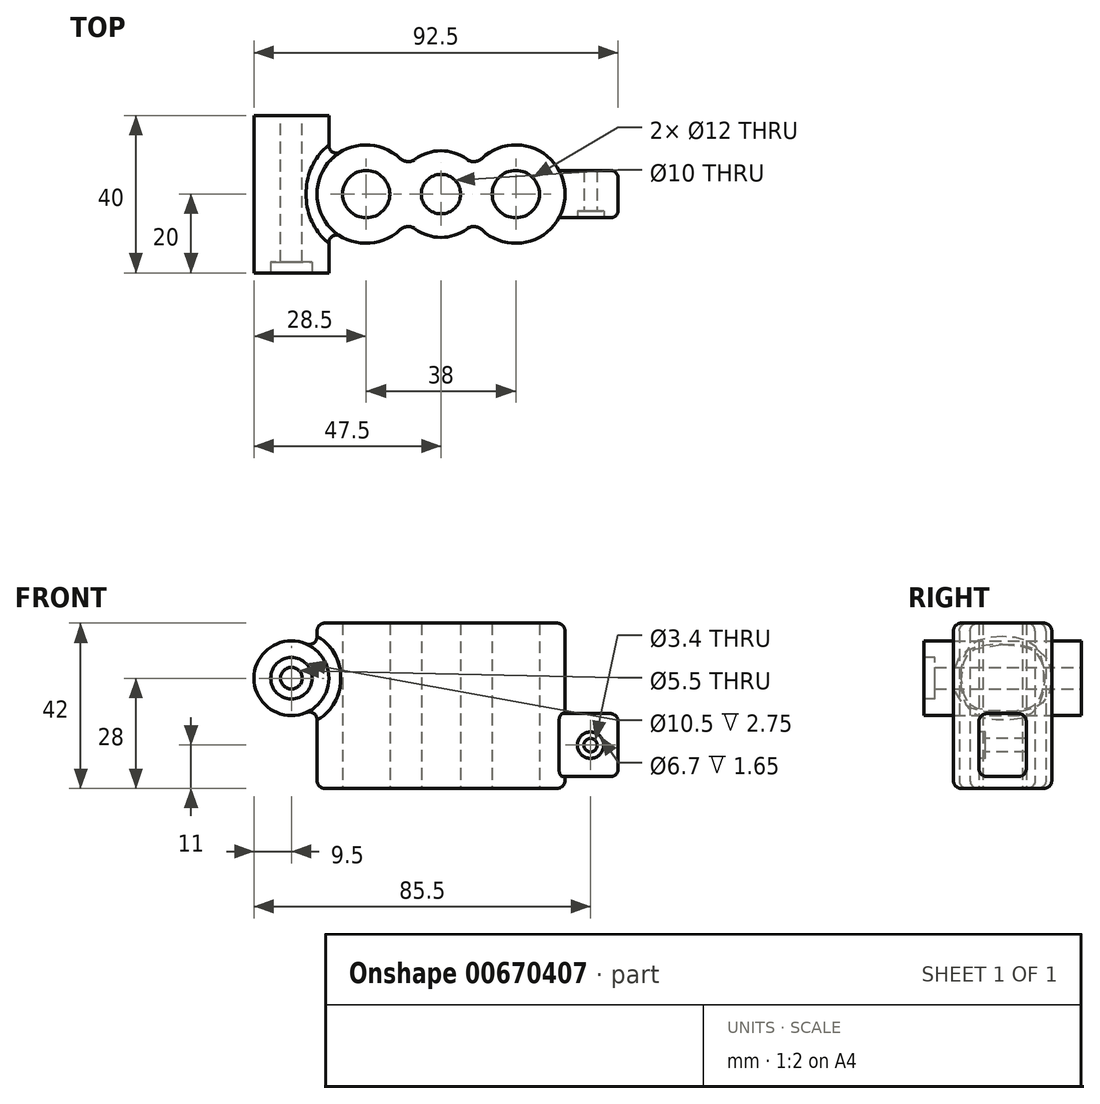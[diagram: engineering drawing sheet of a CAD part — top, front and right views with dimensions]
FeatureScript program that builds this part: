
annotation { "Feature Type Name" : "Feature", "Feature Type Description" : "" }
export const myFeature = defineFeature(function(context is Context, id is Id, definition is map)
    precondition{}
    {
        {
            var Q0;
            Q0=qCreatedBy(makeId("Top.planeOp"),FACE);
            var sketch = newSketch(context, id + "F0", { "sketchPlane" : qUnion([Q0])});
            skLineSegment(sketch, "E0", {"start": v(-22.84, 0) * mm, "end": v(30.08, 0) * mm, "construction": true});
            skLineSegment(sketch, "E1", {"start": v(0, 24.49) * mm, "end": v(0, -24.27) * mm, "construction": true});
            skCircle(sketch, "E2", {"center": v(0, 0) * mm, "radius": 5 * mm});
            skCircle(sketch, "E3", {"center": v(19, 0) * mm, "radius": 6 * mm});
            skCircle(sketch, "E4", {"center": v(-19, 0) * mm, "radius": 6 * mm});
            skArc(sketch, "E5", {"start": v(-10.4, 9.07) * mm, "mid": v(-31.5, 0) * mm, "end": v(-10.4, -9.07) * mm});
            skArc(sketch, "E6", {"start": v(-6.55, -8.84) * mm, "mid": v(0, -11) * mm, "end": v(6.55, -8.84) * mm});
            skArc(sketch, "E7", {"start": v(10.4, -9.07) * mm, "mid": v(31.5, 0) * mm, "end": v(10.4, 9.07) * mm});
            skArc(sketch, "E8.trimOffspring", {"start": v(6.55, 8.84) * mm, "mid": v(0, 11) * mm, "end": v(-6.55, 8.84) * mm});
            skPoint(sketch, "E9.visualSharp", {"position": v(-8.57, 6.9) * mm});
            skArc(sketch, "E9.filletArc", {"start": v(-10.4, 9.07) * mm, "mid": v(-8.52, 8.25) * mm, "end": v(-6.55, 8.84) * mm});
            skPoint(sketch, "E10.visualSharp", {"position": v(8.57, 6.9) * mm});
            skArc(sketch, "E10.filletArc", {"start": v(6.55, 8.84) * mm, "mid": v(8.52, 8.25) * mm, "end": v(10.4, 9.07) * mm});
            skPoint(sketch, "E11.visualSharp", {"position": v(8.57, -6.9) * mm});
            skArc(sketch, "E11.filletArc", {"start": v(10.4, -9.07) * mm, "mid": v(8.52, -8.25) * mm, "end": v(6.55, -8.84) * mm});
            skPoint(sketch, "E12.visualSharp", {"position": v(-8.57, -6.9) * mm});
            skArc(sketch, "E12.filletArc", {"start": v(-6.55, -8.84) * mm, "mid": v(-8.52, -8.25) * mm, "end": v(-10.4, -9.07) * mm});
            skSolve(sketch);
        }
        {
            var Q0;
            Q0=makeQuery(id+"F0.imprint","IMPRINT",FACE,{"disambiguationData":[TD([[makeQuery(id+"F0.imprint","IMPRINT",EDGE,{"derivedFrom":sQuery(id+"F0.wireOp",EDGE,"E2")}),-1.0]])]});
            extrude(context, id + "F1", {"entities" : qUnion([Q0]), "depth" : 42 * mm, "offsetDistance" : 25 * mm});
        }
        {
            var Q0;
            Q0=qCreatedBy(makeId("Front.planeOp"),FACE);
            var sketch = newSketch(context, id + "F2", { "sketchPlane" : qUnion([Q0])});
            skLineSegment(sketch, "E13", {"start": v(-30.33, 0) * mm, "end": v(35.68, 0) * mm, "construction": true});
            skLineSegment(sketch, "E14", {"start": v(0, -22.77) * mm, "end": v(0, 37.59) * mm, "construction": true});
            skCircle(sketch, "E15", {"center": v(-38, 28) * mm, "radius": 2.75 * mm});
            skCircle(sketch, "E16", {"center": v(-38, 28) * mm, "radius": 9.5 * mm});
            skLineSegment(sketch, "E17", {"start": v(-85.83, 21) * mm, "end": v(126.07, 21) * mm, "construction": true});
            skSolve(sketch);
        }
        {
            var Q0;
            Q0=makeQuery(id+"F2.imprint","IMPRINT",FACE,{"disambiguationData":[TD([[makeQuery(id+"F2.imprint","IMPRINT",EDGE,{"derivedFrom":sQuery(id+"F2.wireOp",EDGE,"E15")}),-1.0]])]});
            extrude(context, id + "F3", {"entities" : qUnion([Q0]), "operationType" : NewBodyOperationType.ADD, "endBound" : BoundingType.SYMMETRIC, "depth" : 40 * mm, "offsetDistance" : 25 * mm});
        }
        {
            var Q0;
            Q0=makeQuery(id+"F3.opExtrude","CAP_FACE",FACE,{"disambiguationData":[OSD([sQuery(id+"F2.wireOp",EDGE,"E15"),sQuery(id+"F2.wireOp",EDGE,"E16")])],"isStart":false});
            var sketch = newSketch(context, id + "F4", { "sketchPlane" : qUnion([Q0])});
            skCircle(sketch, "E18", {"center": v(-38, 28) * mm, "radius": 5.25 * mm});
            skSolve(sketch);
        }
        {
            var Q0;
            Q0=makeQuery(id+"F4.imprint","IMPRINT",FACE,{"disambiguationData":[TD([[makeQuery(id+"F4.imprint","IMPRINT",EDGE,{"derivedFrom":sQuery(id+"F4.wireOp",EDGE,"E18")}),1.0]])]});
            var Q1;
            Q1=sQuery(id+"F4.wireOp",EDGE,"E18");
            extrude(context, id + "F5", {"entities" : qUnion([Q0]), "operationType" : NewBodyOperationType.REMOVE, "surfaceEntities" : qUnion([Q1]), "oppositeDirection" : true, "depth" : 2.75 * mm, "offsetDistance" : 25 * mm});
        }
        {
            var Q0;
            Q0=qCreatedBy(makeId("Right.planeOp"),FACE);
            var Q1;
            Q1=sQuery(id+"F4.wireOp",VERTEX,"E18.center");
            cPlane(context, id + "F6", {"entities" : qUnion([Q0, Q1]), "cplaneType" : CPlaneType.PLANE_POINT, "offset" : 25 * mm, "width" : 150 * mm, "height" : 150 * mm});
        }
        {
            var Q0;
            Q0=qCreatedBy(id+"F6.planeOp",FACE);
            cPlane(context, id + "F7", {"entities" : qUnion([Q0]), "cplaneType" : CPlaneType.OFFSET, "offset" : 83 * mm, "width" : 150 * mm, "height" : 150 * mm});
        }
        {
            var Q0;
            Q0=qCreatedBy(id+"F7.planeOp",FACE);
            var sketch = newSketch(context, id + "F8", { "sketchPlane" : qUnion([Q0])});
            skLineSegment(sketch, "E19.bottom", {"start": v(-6, 19) * mm, "end": v(6, 19) * mm});
            skLineSegment(sketch, "E19.top", {"start": v(-6, 3) * mm, "end": v(6, 3) * mm});
            skLineSegment(sketch, "E19.left", {"start": v(-6, 19) * mm, "end": v(-6, 3) * mm});
            skLineSegment(sketch, "E19.right", {"start": v(6, 19) * mm, "end": v(6, 3) * mm});
            skLineSegment(sketch, "E20", {"start": v(0, 59.9) * mm, "end": v(0, -63.49) * mm, "construction": true});
            skSolve(sketch);
        }
        {
            var Q0;
            Q0=makeQuery(id+"F8.imprint","IMPRINT",FACE,{"disambiguationData":[TD([[makeQuery(id+"F8.imprint","IMPRINT",EDGE,{"derivedFrom":sQuery(id+"F8.wireOp",EDGE,"E19.bottom")}),-1.0]])]});
            extrude(context, id + "F9", {"entities" : qUnion([Q0]), "operationType" : NewBodyOperationType.ADD, "endBound" : BoundingType.UP_TO_NEXT, "oppositeDirection" : true, "depth" : 25 * mm, "offsetDistance" : 25 * mm});
        }
        {
            var Q0;
            Q0=makeQuery(id+"F9.opExtrude","SWEPT_FACE",FACE,{"disambiguationData":[OSD([sQuery(id+"F8.wireOp",EDGE,"E19.left")])]});
            var sketch = newSketch(context, id + "F10", { "sketchPlane" : qUnion([Q0])});
            skCircle(sketch, "E21", {"center": v(38, 11) * mm, "radius": 1.7 * mm});
            skSolve(sketch);
        }
        {
            var Q0;
            Q0=makeQuery(id+"F10.imprint","IMPRINT",FACE,{"disambiguationData":[TD([[makeQuery(id+"F10.imprint","IMPRINT",EDGE,{"derivedFrom":sQuery(id+"F10.wireOp",EDGE,"E21")}),1.0]])]});
            extrude(context, id + "F11", {"entities" : qUnion([Q0]), "operationType" : NewBodyOperationType.REMOVE, "endBound" : BoundingType.THROUGH_ALL, "oppositeDirection" : true, "depth" : 25 * mm, "offsetDistance" : 25 * mm});
        }
        {
            var Q0;
            Q0=makeQuery(id+"F9.opExtrude","SWEPT_FACE",FACE,{"disambiguationData":[OSD([sQuery(id+"F8.wireOp",EDGE,"E19.left")])]});
            var sketch = newSketch(context, id + "F12", { "sketchPlane" : qUnion([Q0])});
            skPoint(sketch, "E22.centerSnap0", {"position": v(45, 11) * mm});
            skCircle(sketch, "E23", {"center": v(38, 11) * mm, "radius": 3.35 * mm});
            skSolve(sketch);
        }
        {
            var Q0;
            Q0=makeQuery(id+"F12.imprint","IMPRINT",FACE,{"disambiguationData":[TD([[makeQuery(id+"F12.imprint","IMPRINT",EDGE,{"derivedFrom":sQuery(id+"F12.wireOp",EDGE,"E23")}),1.0]])]});
            extrude(context, id + "F13", {"entities" : qUnion([Q0]), "operationType" : NewBodyOperationType.REMOVE, "oppositeDirection" : true, "depth" : 1.65 * mm, "offsetDistance" : 25 * mm});
        }
        {
            var Q0;
            Q0=makeQuery(id+"F1.opExtrude","CAP_EDGE",EDGE,{"disambiguationData":[OSD([sQuery(id+"F0.wireOp",EDGE,"E7")])],"isStart":false});
            var Q1;
            Q1=makeQuery(id+"F1.opExtrude","CAP_EDGE",EDGE,{"disambiguationData":[OSD([sQuery(id+"F0.wireOp",EDGE,"E7")])],"isStart":true});
            fillet(context, id + "F14", {"entities" : qUnion([Q0, Q1]), "radius" : 2 * mm, "tangentPropagation" : true, "allowEdgeOverflow" : false});
        }
        {
            var Q0;
            Q0=makeQuery(id+"F9.opExtrude","CAP_EDGE",EDGE,{"disambiguationData":[OSD([sQuery(id+"F8.wireOp",EDGE,"E19.left")])],"isStart":true});
            var Q1;
            Q1=makeQuery(id+"F9.opExtrude","SWEPT_EDGE",EDGE,{"disambiguationData":[OSD([sQuery(id+"F8.wireOp",EDGE,"E19.bottom"),sQuery(id+"F8.wireOp",EDGE,"E19.left")])]});
            var Q2;
            Q2=makeQuery(id+"F9.opExtrude","SWEPT_EDGE",EDGE,{"disambiguationData":[OSD([sQuery(id+"F8.wireOp",EDGE,"E19.top"),sQuery(id+"F8.wireOp",EDGE,"E19.left")])]});
            fillet(context, id + "F15", {"entities" : qUnion([Q0, Q1, Q2]), "radius" : 2 * mm, "tangentPropagation" : true, "allowEdgeOverflow" : false});
        }
        {
            var Q0;
            Q0=makeQuery(id+"F9.opExtrude","SWEPT_EDGE",EDGE,{"disambiguationData":[OSD([sQuery(id+"F8.wireOp",EDGE,"E19.top"),sQuery(id+"F8.wireOp",EDGE,"E19.right")])]});
            var Q1;
            Q1=makeQuery(id+"F9.opExtrude","SWEPT_EDGE",EDGE,{"disambiguationData":[OSD([sQuery(id+"F8.wireOp",EDGE,"E19.bottom"),sQuery(id+"F8.wireOp",EDGE,"E19.right")])]});
            var Q2;
            Q2=makeQuery(id+"F9.opExtrude","CAP_EDGE",EDGE,{"disambiguationData":[OSD([sQuery(id+"F8.wireOp",EDGE,"E19.right")])],"isStart":true});
            fillet(context, id + "F16", {"entities" : qUnion([Q0, Q1, Q2]), "radius" : 2 * mm, "tangentPropagation" : true, "allowEdgeOverflow" : false});
        }
        {
            var Q0;
            Q0=makeQuery(id+"F9.opExtrude","CAP_EDGE",EDGE,{"disambiguationData":[OSD([sQuery(id+"F8.wireOp",EDGE,"E19.bottom")])],"isStart":true});
            var Q1;
            Q1=makeQuery(id+"F9.opExtrude","CAP_EDGE",EDGE,{"disambiguationData":[OSD([sQuery(id+"F8.wireOp",EDGE,"E19.top")])],"isStart":true});
            fillet(context, id + "F17", {"entities" : qUnion([Q0, Q1]), "radius" : 2 * mm, "tangentPropagation" : true, "allowEdgeOverflow" : false});
        }
        {
            var Q0;
            Q0=makeQuery(id+"F3.boolean.opBoolean","INTERSECT",EDGE,{"derivedFrom":[makeQuery(id+"F1.opExtrude","SWEPT_FACE",FACE,{"disambiguationData":[OSD([sQuery(id+"F0.wireOp",EDGE,"E5")])]}),makeQuery(id+"F3.opExtrude","SWEPT_FACE",FACE,{"disambiguationData":[OSD([sQuery(id+"F2.wireOp",EDGE,"E16")])]})]});
            fillet(context, id + "F18", {"entities" : qUnion([Q0]), "radius" : 2 * mm, "tangentPropagation" : true, "allowEdgeOverflow" : false});
        }
    });
